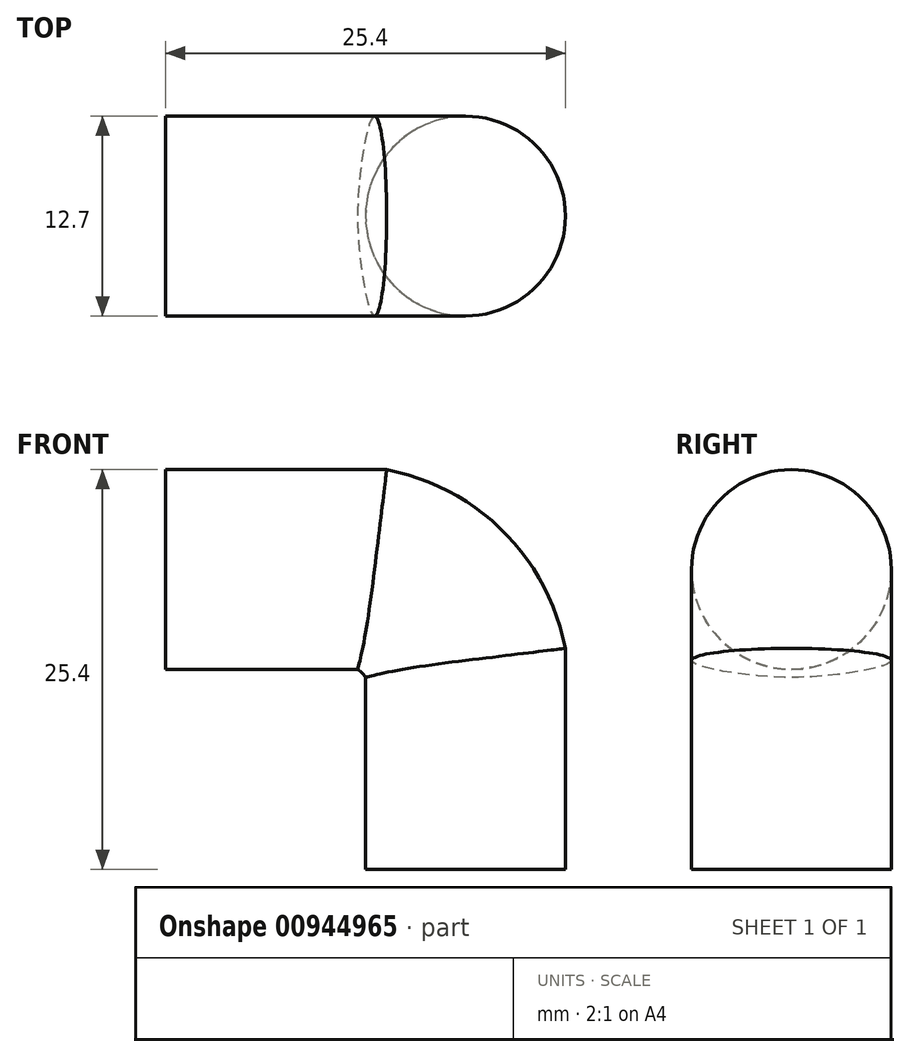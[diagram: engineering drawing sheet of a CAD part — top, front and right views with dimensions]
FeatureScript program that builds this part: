
annotation { "Feature Type Name" : "Feature", "Feature Type Description" : "" }
export const myFeature = defineFeature(function(context is Context, id is Id, definition is map)
    precondition{}
    {
        {
            var Q0;
            Q0=qCreatedBy(makeId("Top.planeOp"),FACE);
            var sketch = newSketch(context, id + "F0", { "sketchPlane" : qUnion([Q0])});
            skCircle(sketch, "E0", {"center": v(0, 0) * mm, "radius": 6.35 * mm});
            skSolve(sketch);
        }
        {
            var Q0;
            Q0=qCreatedBy(makeId("Front.planeOp"),FACE);
            var sketch = newSketch(context, id + "F1", { "sketchPlane" : qUnion([Q0])});
            skLineSegment(sketch, "E1", {"start": v(0, 0) * mm, "end": v(0, 13.27) * mm});
            skLineSegment(sketch, "E2", {"start": v(-5.78, 19.05) * mm, "end": v(-19.05, 19.05) * mm});
            skArc(sketch, "E3", {"start": v(0, 13.27) * mm, "mid": v(-2.08, 16.97) * mm, "end": v(-5.78, 19.05) * mm});
            skPoint(sketch, "E4.orphan", {"position": v(-9.53, 19.05) * mm});
            skPoint(sketch, "E5.orphan", {"position": v(0, 19.05) * mm});
            skPoint(sketch, "E6.orphan", {"position": v(0, 9.53) * mm});
            skSolve(sketch);
        }
        {
            var Q0;
            Q0=makeQuery(id+"F0.imprint","IMPRINT",FACE,{"disambiguationData":[TD([[makeQuery(id+"F0.imprint","IMPRINT",EDGE,{"derivedFrom":sQuery(id+"F0.wireOp",EDGE,"E0")}),1.0]])]});
            var Q1;
            Q1=sQuery(id+"F1.wireOp",EDGE,"E2");
            var Q2;
            Q2=sQuery(id+"F1.wireOp",EDGE,"E3");
            var Q3;
            Q3=sQuery(id+"F1.wireOp",EDGE,"E1");
            sweep(context, id + "F2", {"profiles" : qUnion([Q0]), "path" : qUnion([Q1, Q2, Q3])});
        }
    });
